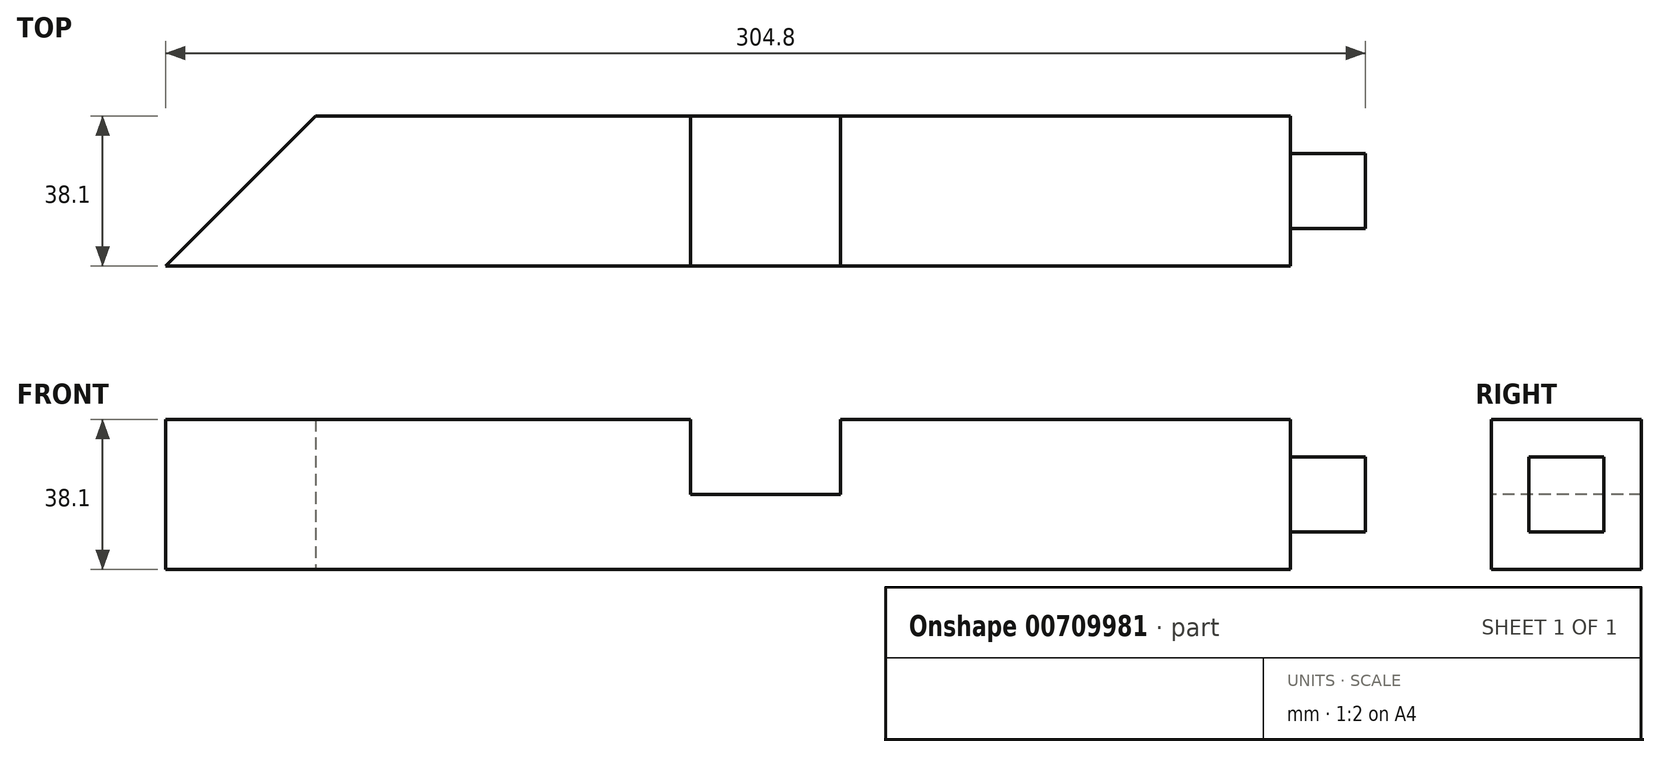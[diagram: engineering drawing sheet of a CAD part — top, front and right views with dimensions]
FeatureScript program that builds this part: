
annotation { "Feature Type Name" : "Feature", "Feature Type Description" : "" }
export const myFeature = defineFeature(function(context is Context, id is Id, definition is map)
    precondition{}
    {
        {
            var Q0;
            Q0=qCreatedBy(makeId("Top.planeOp"),FACE);
            var sketch = newSketch(context, id + "F0", { "sketchPlane" : qUnion([Q0])});
            skLineSegment(sketch, "E0.bottom", {"start": v(152.4, 19.05) * mm, "end": v(-114.3, 19.05) * mm});
            skLineSegment(sketch, "E0.top", {"start": v(152.4, -19.05) * mm, "end": v(-152.4, -19.05) * mm});
            skLineSegment(sketch, "E0.left", {"start": v(152.4, 19.05) * mm, "end": v(152.4, -19.05) * mm});
            skPoint(sketch, "E0.middle", {"position": v(0, 0) * mm});
            skPoint(sketch, "E1", {"position": v(-114.3, 19.05) * mm});
            skLineSegment(sketch, "E2", {"start": v(-152.4, -19.05) * mm, "end": v(-114.3, 19.05) * mm});
            skSolve(sketch);
        }
        {
            var Q0;
            Q0=qSketchRegion(id+"F0",true);
            extrude(context, id + "F1", {"entities" : qUnion([Q0]), "endBound" : BoundingType.SYMMETRIC, "depth" : 38.1 * mm, "offsetDistance" : 25.4 * mm});
        }
        {
            var Q0;
            Q0=qCreatedBy(makeId("Top.planeOp"),FACE);
            var sketch = newSketch(context, id + "F2", { "sketchPlane" : qUnion([Q0])});
            skLineSegment(sketch, "E3.bottom", {"start": v(19.05, 19.05) * mm, "end": v(-19.05, 19.05) * mm});
            skLineSegment(sketch, "E3.top", {"start": v(19.05, -19.05) * mm, "end": v(-19.05, -19.05) * mm});
            skLineSegment(sketch, "E3.left", {"start": v(19.05, 19.05) * mm, "end": v(19.05, -19.05) * mm});
            skLineSegment(sketch, "E3.right", {"start": v(-19.05, 19.05) * mm, "end": v(-19.05, -19.05) * mm});
            skPoint(sketch, "E3.middle", {"position": v(0, 0) * mm});
            skSolve(sketch);
        }
        {
            var Q0;
            Q0=qSketchRegion(id+"F2",true);
            extrude(context, id + "F3", {"entities" : qUnion([Q0]), "operationType" : NewBodyOperationType.REMOVE, "depth" : 19.05 * mm, "offsetDistance" : 25.4 * mm});
        }
        {
            var Q0;
            Q0=makeQuery(id+"F1.opExtrude","SWEPT_FACE",FACE,{"disambiguationData":[OSD([sQuery(id+"F0.wireOp",EDGE,"E0.left")])]});
            var sketch = newSketch(context, id + "F4", { "sketchPlane" : qUnion([Q0])});
            skLineSegment(sketch, "E4.bottom", {"start": v(19.05, 19.05) * mm, "end": v(-19.05, 19.05) * mm});
            skLineSegment(sketch, "E4.top", {"start": v(19.05, -19.05) * mm, "end": v(-19.05, -19.05) * mm});
            skLineSegment(sketch, "E4.left", {"start": v(19.05, 19.05) * mm, "end": v(19.05, -19.05) * mm});
            skLineSegment(sketch, "E4.right", {"start": v(-19.05, 19.05) * mm, "end": v(-19.05, -19.05) * mm});
            skPoint(sketch, "E4.middle", {"position": v(0, 0) * mm});
            skLineSegment(sketch, "E5.bottom", {"start": v(9.53, 9.52) * mm, "end": v(-9.52, 9.52) * mm});
            skLineSegment(sketch, "E5.top", {"start": v(9.52, -9.53) * mm, "end": v(-9.53, -9.52) * mm});
            skLineSegment(sketch, "E5.left", {"start": v(9.53, 9.52) * mm, "end": v(9.52, -9.53) * mm});
            skLineSegment(sketch, "E5.right", {"start": v(-9.52, 9.52) * mm, "end": v(-9.53, -9.52) * mm});
            skSolve(sketch);
        }
        {
            var Q0;
            Q0 = qSketchRegion(id + "F4", true);
            extrude(context, id + "F5", {"entities" : qUnion([Q0]), "operationType" : NewBodyOperationType.REMOVE, "oppositeDirection" : true, "depth" : 19.05 * mm, "offsetDistance" : 25.4 * mm});
        }
    });
